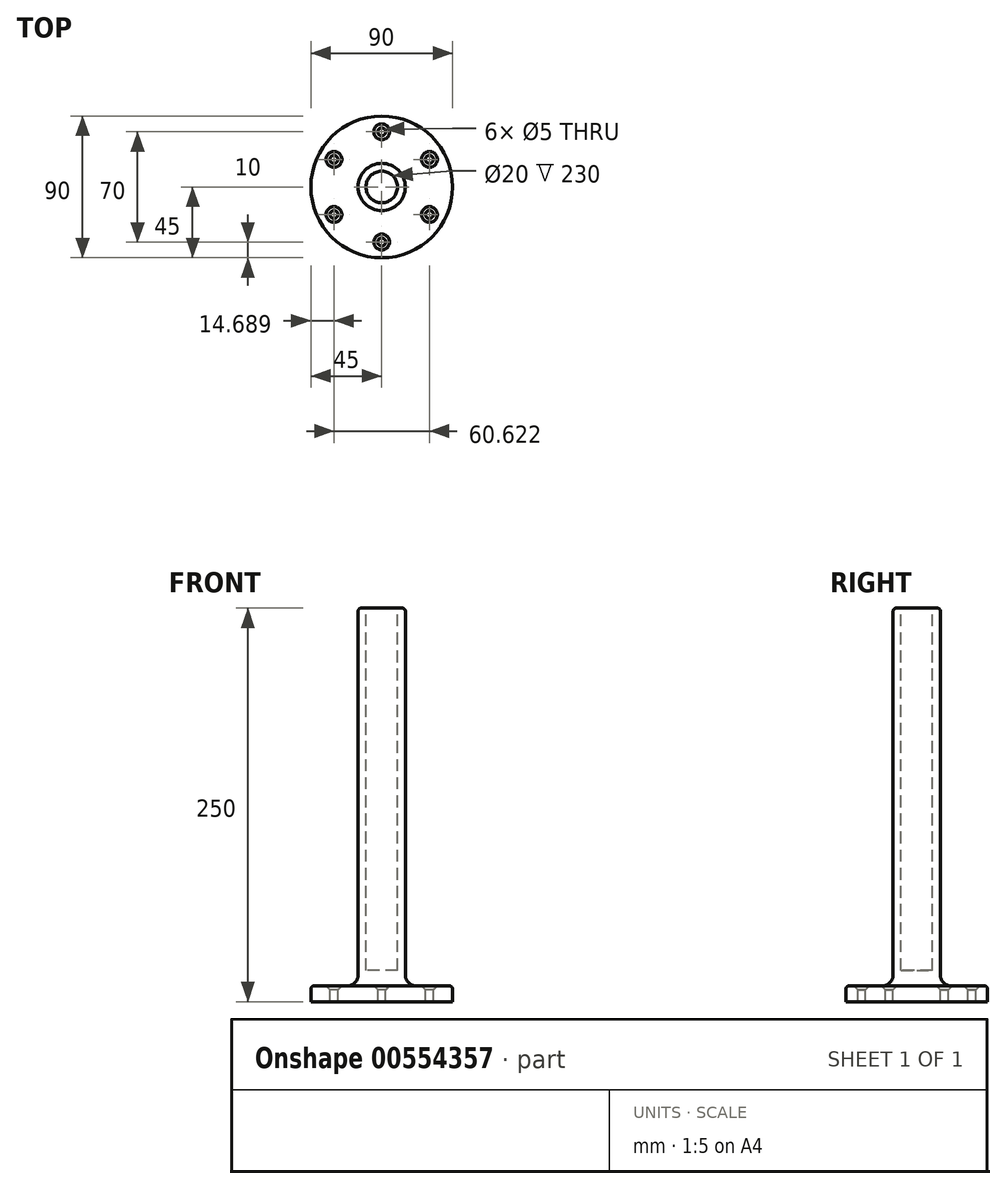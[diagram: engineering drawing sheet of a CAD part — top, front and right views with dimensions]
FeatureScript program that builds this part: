
annotation { "Feature Type Name" : "Feature", "Feature Type Description" : "" }
export const myFeature = defineFeature(function(context is Context, id is Id, definition is map)
    precondition{}
    {
        {
            var Q0;
            Q0=qCreatedBy(makeId("Top.planeOp"),FACE);
            var sketch = newSketch(context, id + "F0", { "sketchPlane" : qUnion([Q0])});
            skCircle(sketch, "E0", {"center": v(0, 0) * mm, "radius": 45 * mm});
            skSolve(sketch);
        }
        {
            var Q0;
            Q0=makeQuery(id+"F0.imprint","IMPRINT",FACE,{"disambiguationData":[TD([[makeQuery(id+"F0.imprint","IMPRINT",EDGE,{"derivedFrom":sQuery(id+"F0.wireOp",EDGE,"E0")}),1.0]])]});
            extrude(context, id + "F1", {"entities" : qUnion([Q0]), "depth" : 10 * mm, "offsetDistance" : 25.4 * mm});
        }
        {
            var Q0;
            Q0=qCreatedBy(makeId("Top.planeOp"),FACE);
            var sketch = newSketch(context, id + "F2", { "sketchPlane" : qUnion([Q0])});
            skCircle(sketch, "E1", {"center": v(0, 0) * mm, "radius": 15 * mm});
            skSolve(sketch);
        }
        {
            var Q0;
            Q0=qSketchRegion(id+"F2",true);
            extrude(context, id + "F3", {"entities" : qUnion([Q0]), "operationType" : NewBodyOperationType.ADD, "depth" : 250 * mm, "offsetDistance" : 25 * mm});
        }
        {
            var Q0;
            Q0=makeQuery(id+"F1.opExtrude","CAP_FACE",FACE,{"disambiguationData":[OSD([sQuery(id+"F0.wireOp",EDGE,"E0")])],"isStart":false});
            var sketch = newSketch(context, id + "F4", { "sketchPlane" : qUnion([Q0])});
            skCircle(sketch, "E2", {"center": v(0, 35) * mm, "radius": 4.5 * mm});
            skCircle(sketch, "E3.1.0", {"center": v(-30.31, 17.5) * mm, "radius": 4.5 * mm});
            skCircle(sketch, "E3.2.0", {"center": v(-30.31, -17.5) * mm, "radius": 4.5 * mm});
            skCircle(sketch, "E3.3.0", {"center": v(0, -35) * mm, "radius": 4.5 * mm});
            skCircle(sketch, "E3.4.0", {"center": v(30.31, -17.5) * mm, "radius": 4.5 * mm});
            skCircle(sketch, "E3.5.0", {"center": v(30.31, 17.5) * mm, "radius": 4.5 * mm});
            skPoint(sketch, "E3.center", {"position": v(0, 0) * mm});
            skLineSegment(sketch, "E4", {"start": v(0, 0) * mm, "end": v(0, 35) * mm});
            skSolve(sketch);
        }
        {
            var Q0;
            Q0=sQuery(id+"F4.wireOp",VERTEX,"E2.center");
            var Q1;
            Q1=sQuery(id+"F4.wireOp",VERTEX,"E3.1.0.center");
            var Q2;
            Q2=sQuery(id+"F4.wireOp",VERTEX,"E3.2.0.center");
            var Q3;
            Q3=sQuery(id+"F4.wireOp",VERTEX,"E3.3.0.center");
            var Q4;
            Q4=sQuery(id+"F4.wireOp",VERTEX,"E3.4.0.center");
            var Q5;
            Q5=sQuery(id+"F4.wireOp",VERTEX,"E3.5.0.center");
            var Q6;
            Q6=makeQuery(id+"F1.opExtrude","SWEPT_BODY",BODY,{"disambiguationData":[OSD([sQuery(id+"F0.wireOp",EDGE,"E0")])]});
            hole(context, id + "F5", {"style" : HoleStyle.C_SINK, "endStyle" : HoleEndStyle.THROUGH, "holeDiameter" : 5 * mm, "cSinkDiameter" : 10 * mm, "cSinkAngle" : 90 * degree, "isTappedThrough" : true, "tappedDepth" : 12 * mm, "tapClearance" : 3, "locations" : qUnion([Q0, Q1, Q2, Q3, Q4, Q5]), "scope" : qUnion([Q6])});
        }
        {
            var Q0;
            Q0=makeQuery(id+"F3.boolean.opBoolean","INTERSECT",EDGE,{"derivedFrom":[makeQuery(id+"F1.opExtrude","CAP_FACE",FACE,{"disambiguationData":[OSD([sQuery(id+"F0.wireOp",EDGE,"E0")])],"isStart":false}),makeQuery(id+"F3.opExtrude","SWEPT_FACE",FACE,{"disambiguationData":[OSD([sQuery(id+"F2.wireOp",EDGE,"E1")])]})]});
            fillet(context, id + "F6", {"entities" : qUnion([Q0]), "radius" : 7 * mm, "tangentPropagation" : true, "allowEdgeOverflow" : false});
        }
        {
            var Q0;
            Q0=makeQuery(id+"F3.opExtrude","CAP_EDGE",EDGE,{"disambiguationData":[OSD([sQuery(id+"F2.wireOp",EDGE,"E1")])],"isStart":false});
            fillet(context, id + "F7", {"entities" : qUnion([Q0]), "radius" : 2 * mm, "tangentPropagation" : true, "allowEdgeOverflow" : false});
        }
        {
            var Q0;
            Q0=makeQuery(id+"F1.opExtrude","CAP_EDGE",EDGE,{"disambiguationData":[OSD([sQuery(id+"F0.wireOp",EDGE,"E0")])],"isStart":false});
            fillet(context, id + "F8", {"entities" : qUnion([Q0]), "radius" : 2 * mm, "tangentPropagation" : true, "allowEdgeOverflow" : false});
        }
        {
            var Q0;
            Q0=makeQuery(id+"F3.opExtrude","CAP_FACE",FACE,{"disambiguationData":[OSD([sQuery(id+"F2.wireOp",EDGE,"E1")])],"isStart":false});
            var sketch = newSketch(context, id + "F9", { "sketchPlane" : qUnion([Q0])});
            skSolve(sketch);
        }
        {
            var Q0;
            {var subQ0=sQuery(id+"F2.wireOp",EDGE,"E1");Q0=makeQuery(id+"F9.imprint","IMPRINT",FACE,{"disambiguationData":[TD([[makeQuery(id+"F9.imprint","IMPRINT",EDGE,{"derivedFrom":makeQuery(id+"F7.opFillet","BLEND_EDGE",EDGE,{"blendedFrom":[makeQuery(id+"F3.opExtrude","CAP_EDGE",EDGE,{"disambiguationData":[OSD([subQ0])],"isStart":false}),makeQuery(id+"F3.opExtrude","CAP_FACE",FACE,{"disambiguationData":[OSD([subQ0])],"isStart":false})],"blendedInto":[makeQuery(id+"F3.opExtrude","CAP_FACE",FACE,{"disambiguationData":[OSD([subQ0])],"isStart":false})]})}),1.0]])]});}
            var sketch = newSketch(context, id + "F10", { "sketchPlane" : qUnion([Q0])});
            skCircle(sketch, "E5", {"center": v(0, 0) * mm, "radius": 10 * mm});
            skSolve(sketch);
        }
        {
            var Q0;
            Q0 = qSketchRegion(id + "F10", true);
            extrude(context, id + "F11", {"entities" : qUnion([Q0]), "operationType" : NewBodyOperationType.REMOVE, "oppositeDirection" : true, "depth" : 230 * mm, "offsetDistance" : 25 * mm});
        }
    });
